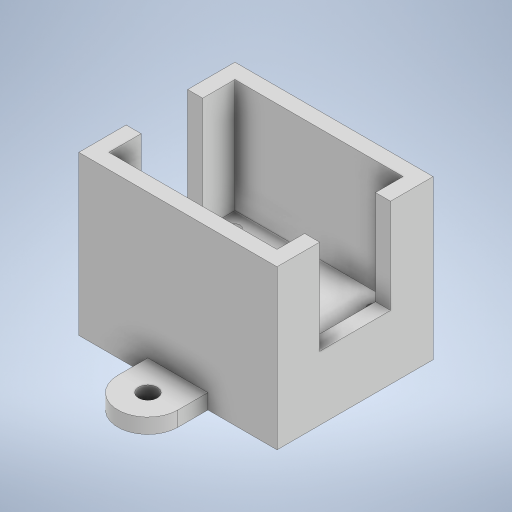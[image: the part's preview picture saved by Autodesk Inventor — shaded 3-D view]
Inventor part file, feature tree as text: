
AUTODESK INVENTOR PART (.ipt)
format: ipt  version: 2024 (Build 280153000, 153)  size: 348,672 bytes
history: native  units: in
note: dims shown in document units (in); Inventor stores cm internally (conversion verified against a paired STEP export)
features: extrude x7, sketch x7, projected_geometry x5
ambient origin geometry x8: Origin, YZ Plane, XZ Plane, XY Plane, X Axis, Y Axis, Z Axis, Center Point
bodies: Solid1 (feature_tree)
feature tree (19):
  extrude  "Extrusion1"  Depth=1.0in
  extrude  "Extrusion2"  Depth=0.1in
  extrude  "Extrusion3"  Depth=0.1in
  extrude  "Extrusion4"  Depth=0.1in
  extrude  "Extrusion5"  Depth=0.1in
  extrude  "Extrusion6"  Depth=0.086in
  extrude  "Extrusion7"  Depth=0.125in
  sketch  "Sketch1"  dims[d0=1.35in d1=1.0in]
  sketch  "Sketch2"  dims[d2=0.1in d3=0.1in]
  projected_geometry  "Projected Loop1"
  sketch  "Sketch3"  dims[d4=0.1in d5=0.1in]
  sketch  "Sketch4"  dims[d6=0.1in d7=0.1in]
  sketch  "Sketch5"  dims[d8=0.1in d9=0.1in]
  projected_geometry  "Projected Loop2"
  sketch  "Sketch6"  dims[d10=0.086in d11=0.086in]
  projected_geometry  "Projected Loop3"
  sketch  "Sketch7"  dims[d12=0.086in d13=0.086in d14=0.025in d15=0.125in d16=0.0in d17=0.125in d18=0.9449in d19=0.125in d20=0.0in d21=0.0in d22=0.2953in d23=0.5906in d24=0.9449in d25=0.0in d26=0.2559in d27=0.5118in d28=0.9449in d29=0.0in d30=0.125in d31=0.25in d32=0.25in d33=0.1575in d34=0.1575in d35=0.25in d36=0.0in d37=0.1575in d38=0.0in d39=0.125in d40=0.0in]
  projected_geometry  "Projected Loop4"
  projected_geometry  "Projected Loop5"
